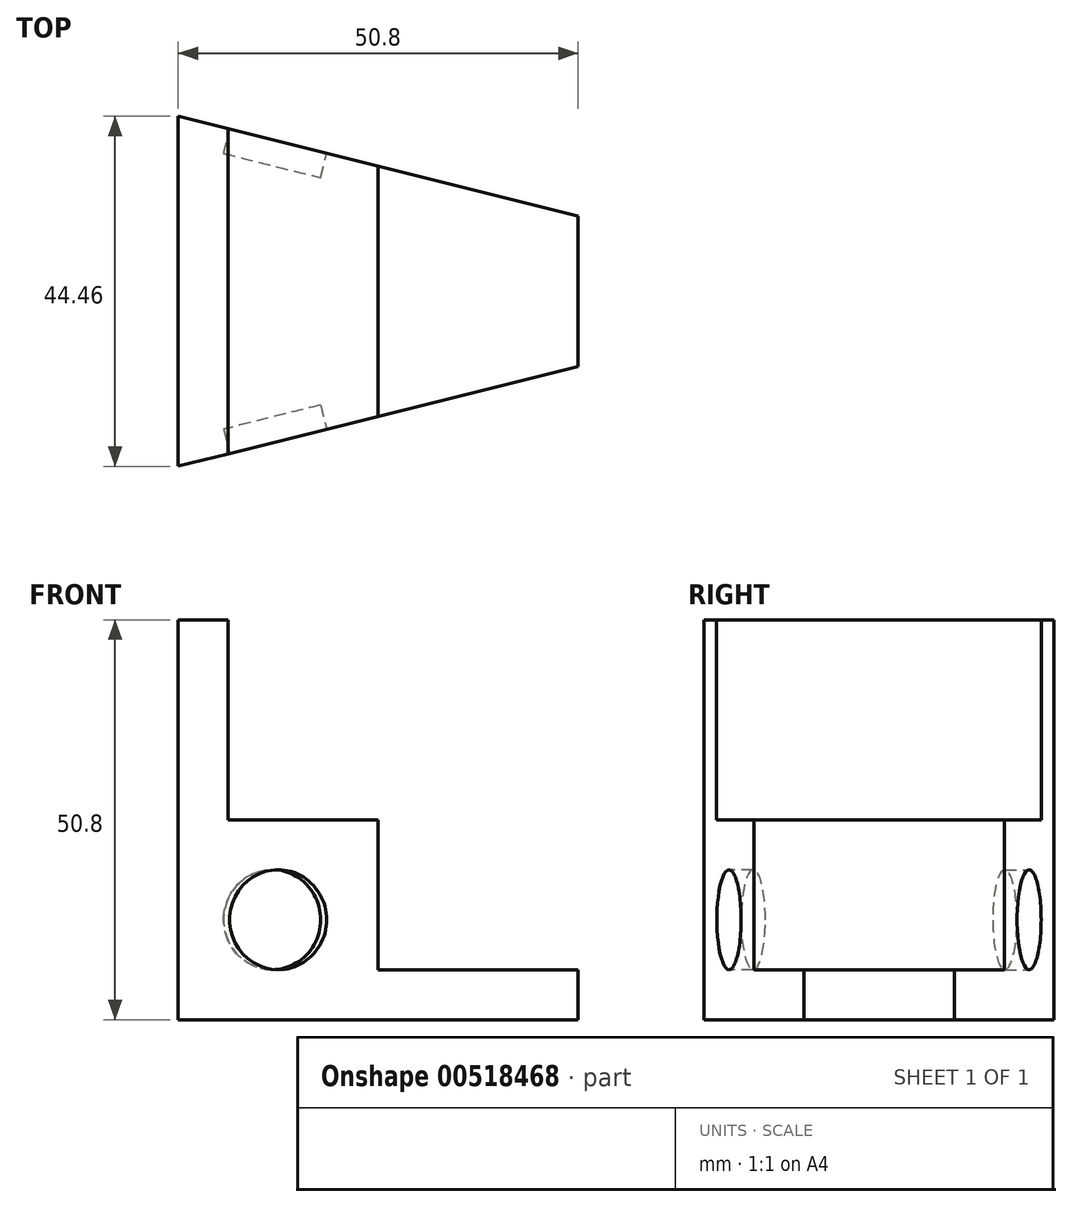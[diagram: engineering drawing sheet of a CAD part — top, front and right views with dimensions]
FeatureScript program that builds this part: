
annotation { "Feature Type Name" : "Feature", "Feature Type Description" : "" }
export const myFeature = defineFeature(function(context is Context, id is Id, definition is map)
    precondition{}
    {
        {
            var Q0;
            Q0=qCreatedBy(makeId("Front.planeOp"),FACE);
            var sketch = newSketch(context, id + "F0", { "sketchPlane" : qUnion([Q0])});
            skLineSegment(sketch, "E0", {"start": v(0, 0) * mm, "end": v(50.8, 0) * mm});
            skLineSegment(sketch, "E1", {"start": v(50.8, 0) * mm, "end": v(50.8, 6.35) * mm});
            skLineSegment(sketch, "E2", {"start": v(50.8, 6.35) * mm, "end": v(25.4, 6.35) * mm});
            skLineSegment(sketch, "E3", {"start": v(25.4, 6.35) * mm, "end": v(25.4, 25.4) * mm});
            skLineSegment(sketch, "E4", {"start": v(25.4, 25.4) * mm, "end": v(6.35, 25.4) * mm});
            skLineSegment(sketch, "E5", {"start": v(6.35, 25.4) * mm, "end": v(6.35, 50.8) * mm});
            skLineSegment(sketch, "E6", {"start": v(6.35, 50.8) * mm, "end": v(0, 50.8) * mm});
            skLineSegment(sketch, "E7", {"start": v(0, 50.8) * mm, "end": v(0, 0) * mm});
            skSolve(sketch);
        }
        {
            var Q0;
            Q0=qSketchRegion(id+"F0",true);
            extrude(context, id + "F1", {"entities" : qUnion([Q0]), "endBound" : BoundingType.SYMMETRIC, "depth" : 44.45 * mm, "offsetDistance" : 25.4 * mm});
        }
        {
            var Q0;
            Q0=makeQuery(id+"F1.opExtrude","SWEPT_FACE",FACE,{"disambiguationData":[OSD([sQuery(id+"F0.wireOp",EDGE,"E0")])]});
            var sketch = newSketch(context, id + "F2", { "sketchPlane" : qUnion([Q0])});
            skLineSegment(sketch, "E8", {"start": v(0, 22.23) * mm, "end": v(50.8, 9.56) * mm});
            skLineSegment(sketch, "E9", {"start": v(0, -22.23) * mm, "end": v(50.8, -9.56) * mm});
            skLineSegment(sketch, "E10", {"start": v(50.8, -9.56) * mm, "end": v(50.8, 9.56) * mm});
            skLineSegment(sketch, "E11", {"start": v(0, -22.23) * mm, "end": v(0, 22.23) * mm});
            skSolve(sketch);
        }
        {
            var Q0;
            {var subQ0=sQuery(id+"F2.wireOp",EDGE,"E8");Q0=makeQuery(id+"F2.imprint","IMPRINT",FACE,{"disambiguationData":[TD([[makeQuery(id+"F2.imprint","IMPRINT",EDGE,{"derivedFrom":subQ0}),1.0]])]});}
            var Q1;
            {var subQ0=sQuery(id+"F2.wireOp",EDGE,"E9");Q1=makeQuery(id+"F2.imprint","IMPRINT",FACE,{"disambiguationData":[TD([[makeQuery(id+"F2.imprint","IMPRINT",EDGE,{"derivedFrom":subQ0}),-1.0]])]});}
            extrude(context, id + "F3", {"entities" : qUnion([Q0, Q1]), "operationType" : NewBodyOperationType.REMOVE, "endBound" : BoundingType.THROUGH_ALL, "oppositeDirection" : true, "depth" : 25.4 * mm, "offsetDistance" : 25.4 * mm});
        }
        {
            var Q0;
            Q0=makeQuery(id+"F3.boolean.opBoolean","COPY",FACE,{"derivedFrom":makeQuery(id+"F3.opExtrude","SWEPT_FACE",FACE,{"disambiguationData":[OSD([sQuery(id+"F2.wireOp",EDGE,"E8")])]})});
            var sketch = newSketch(context, id + "F4", { "sketchPlane" : qUnion([Q0])});
            skLineSegment(sketch, "E12", {"start": v(20.8, 25.4) * mm, "end": v(-5.38, 0) * mm, "construction": true});
            skPoint(sketch, "E13", {"position": v(7.71, 12.7) * mm});
            skCircle(sketch, "E14", {"center": v(7.71, 12.7) * mm, "radius": 6.35 * mm});
            skSolve(sketch);
        }
        {
            var Q0;
            Q0=makeQuery(id+"F4.imprint","IMPRINT",FACE,{"disambiguationData":[TD([[makeQuery(id+"F4.imprint","IMPRINT",EDGE,{"derivedFrom":sQuery(id+"F4.wireOp",EDGE,"E14")}),1.0]])]});
            extrude(context, id + "F5", {"entities" : qUnion([Q0]), "operationType" : NewBodyOperationType.REMOVE, "oppositeDirection" : true, "depth" : 3.17 * mm, "offsetDistance" : 25.4 * mm});
        }
        {
            var Q0;
            Q0=makeQuery(id+"F3.boolean.opBoolean","COPY",FACE,{"derivedFrom":makeQuery(id+"F3.opExtrude","SWEPT_FACE",FACE,{"disambiguationData":[OSD([sQuery(id+"F2.wireOp",EDGE,"E9")])]})});
            var sketch = newSketch(context, id + "F6", { "sketchPlane" : qUnion([Q0])});
            skLineSegment(sketch, "E15", {"start": v(-20.8, 25.4) * mm, "end": v(5.38, 0) * mm, "construction": true});
            skCircle(sketch, "E16", {"center": v(-7.71, 12.7) * mm, "radius": 6.35 * mm});
            skSolve(sketch);
        }
        {
            var Q0;
            Q0 = qSketchRegion(id + "F6", true);
            extrude(context, id + "F7", {"entities" : qUnion([Q0]), "operationType" : NewBodyOperationType.REMOVE, "oppositeDirection" : true, "depth" : 3.17 * mm, "offsetDistance" : 25.4 * mm});
        }
    });
